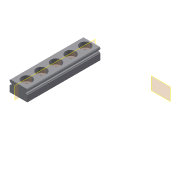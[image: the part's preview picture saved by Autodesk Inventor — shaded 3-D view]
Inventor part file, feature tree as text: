
AUTODESK INVENTOR PART (.ipt)
format: ipt  version: 2019.4 (Build 234330000, 330)  size: 190,464 bytes
history: native  units: mm
features: plane x2, sketch x2, other x2, extrude x1, mirror x1, hole x1, pattern_linear x1, projected_geometry x1
ambient origin geometry x8: Origin, YZ Plane, XZ Plane, XY Plane, X Axis, Y Axis, Z Axis, Center Point
bodies: Solid1 (feature_tree)
feature tree (11):
  plane  "Work Plane1"
  extrude  "Extrusion1"  Depth=0.5mm
  mirror  "Mirror1"
  hole  "Hole1"  [1 undecoded]
  pattern_linear  "Rectangular Pattern1"  Spacing1=6.05mm  [1 undecoded]
  plane  "Work Plane2"
  sketch  "Sketch1"  dims[d0=0.5mm d1=0.5mm]
  sketch  "Sketch2"  dims[d4=50.0mm d5=0.0mm d6=3.5mm d7=6.0mm d8=7.0mm d9=3.5mm d10=90.0deg d11=8.0mm d12=20.594885mm d13=50.0mm d15=10.0mm d17=6.05mm d18=7.8mm d20=2.67563mm d21=0.5mm d22=1.1mm d23=4.7mm d24=0.227539mm d25=0.228mm d26=0.0mm d27=0.248315mm d28=0.218573mm]
  projected_geometry  "Projected Loop1"
  other  "Assembly_Cube_Z_Focus_MGN_NEMA_v3.iam"
  other  "00_MGN12 LINEAR GUIDE RAIL, CONFIGURABLE:1"
note: 2 required parameter values undecoded (feature->parameter linkage not recoverable at this tier; creation-order binding heuristic only, values carry confidence <= 0.55)
